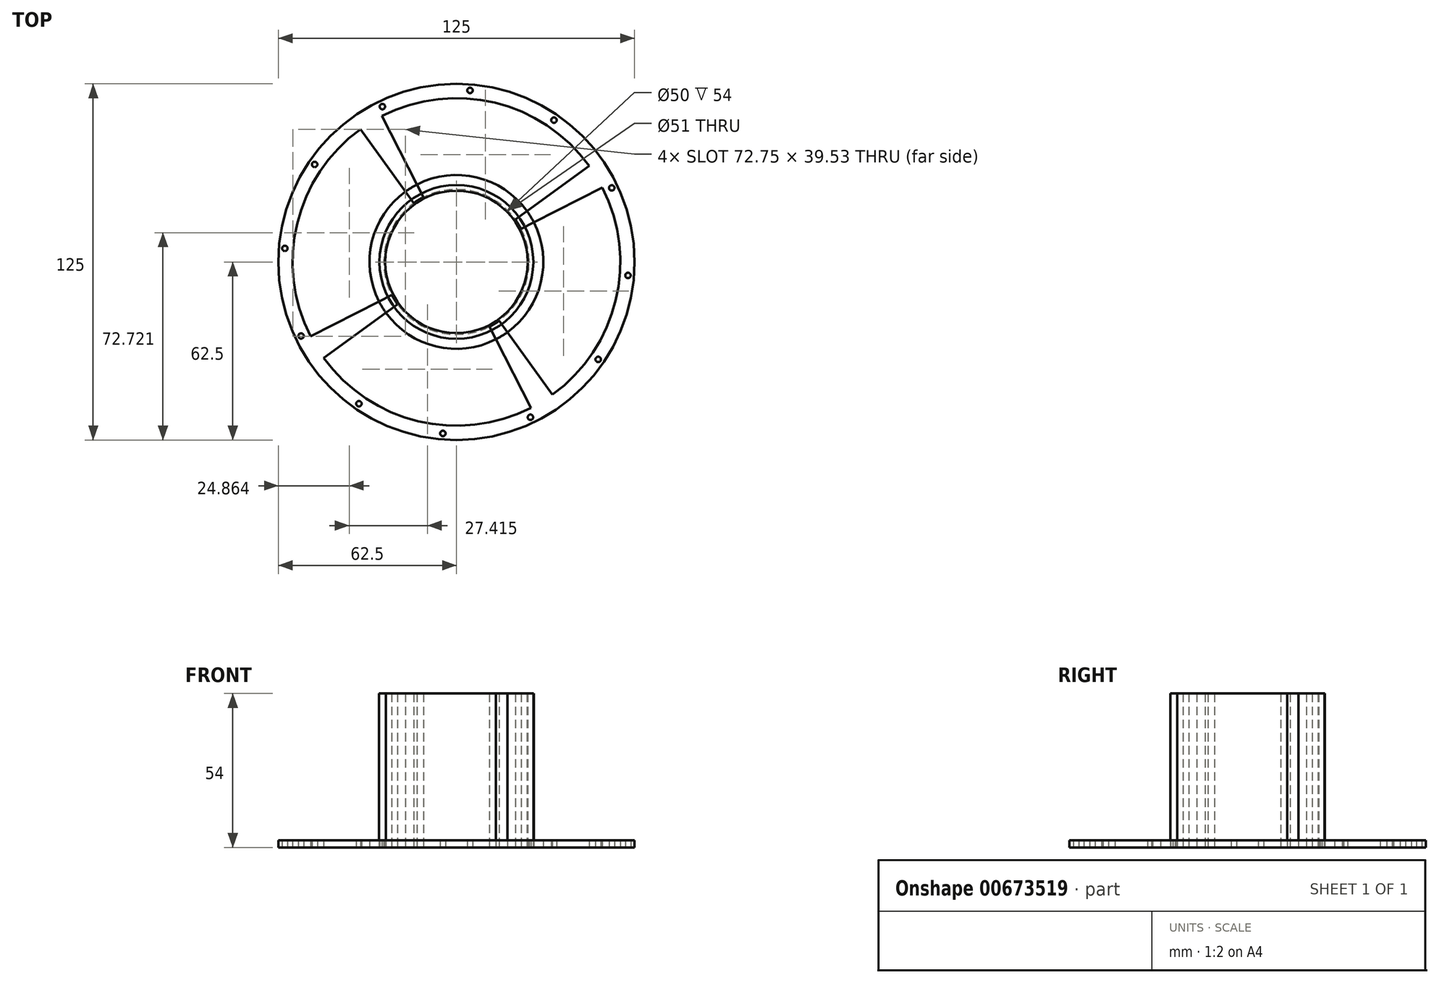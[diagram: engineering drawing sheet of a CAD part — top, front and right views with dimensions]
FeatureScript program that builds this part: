
annotation { "Feature Type Name" : "Feature", "Feature Type Description" : "" }
export const myFeature = defineFeature(function(context is Context, id is Id, definition is map)
    precondition{}
    {
        {
            var Q0;
            Q0=qCreatedBy(makeId("Top.planeOp"),FACE);
            var sketch = newSketch(context, id + "F0", { "sketchPlane" : qUnion([Q0])});
            skCircle(sketch, "E0", {"center": v(0, 0) * mm, "radius": 25.5 * mm});
            skCircle(sketch, "E1.0", {"center": v(0, 0) * mm, "radius": 30.5 * mm});
            skCircle(sketch, "E2", {"center": v(0, 0) * mm, "radius": 57.5 * mm});
            skCircle(sketch, "E3.0", {"center": v(0, 0) * mm, "radius": 62.5 * mm});
            skLineSegment(sketch, "E4", {"start": v(0, 0) * mm, "end": v(51.2, 26.15) * mm});
            skLineSegment(sketch, "E5", {"start": v(0, 0) * mm, "end": v(46.6, 33.7) * mm});
            skLineSegment(sketch, "E6.1.0", {"start": v(0, 0) * mm, "end": v(-33.7, 46.6) * mm});
            skLineSegment(sketch, "E6.1.1", {"start": v(0, 0) * mm, "end": v(-26.15, 51.2) * mm});
            skLineSegment(sketch, "E6.2.0", {"start": v(0, 0) * mm, "end": v(-46.6, -33.7) * mm});
            skLineSegment(sketch, "E6.2.1", {"start": v(0, 0) * mm, "end": v(-51.2, -26.15) * mm});
            skLineSegment(sketch, "E6.3.0", {"start": v(0, 0) * mm, "end": v(33.7, -46.6) * mm});
            skLineSegment(sketch, "E6.3.1", {"start": v(0, 0) * mm, "end": v(26.15, -51.2) * mm});
            skCircle(sketch, "E7", {"center": v(34.22, 49.76) * mm, "radius": 0.95 * mm});
            skCircle(sketch, "E8.1.0", {"center": v(4.76, 60.2) * mm, "radius": 0.95 * mm});
            skCircle(sketch, "E8.2.0", {"center": v(-25.98, 54.52) * mm, "radius": 0.95 * mm});
            skCircle(sketch, "E8.3.0", {"center": v(-49.76, 34.22) * mm, "radius": 0.95 * mm});
            skCircle(sketch, "E8.4.0", {"center": v(-60.2, 4.76) * mm, "radius": 0.95 * mm});
            skCircle(sketch, "E8.5.0", {"center": v(-54.52, -25.98) * mm, "radius": 0.95 * mm});
            skCircle(sketch, "E8.6.0", {"center": v(-34.22, -49.76) * mm, "radius": 0.95 * mm});
            skCircle(sketch, "E8.7.0", {"center": v(-4.76, -60.2) * mm, "radius": 0.95 * mm});
            skCircle(sketch, "E8.8.0", {"center": v(25.98, -54.52) * mm, "radius": 0.95 * mm});
            skCircle(sketch, "E8.9.0", {"center": v(49.76, -34.22) * mm, "radius": 0.95 * mm});
            skCircle(sketch, "E8.10.0", {"center": v(60.2, -4.76) * mm, "radius": 0.95 * mm});
            skCircle(sketch, "E8.11.0", {"center": v(54.52, 25.98) * mm, "radius": 0.95 * mm});
            skSolve(sketch);
        }
        {
            var Q0;
            Q0=makeQuery(id+"F0.imprint","IMPRINT",FACE,{"disambiguationData":[TD([[makeQuery(id+"F0.imprint","IMPRINT",EDGE,{"derivedFrom":sQuery(id+"F0.wireOp",EDGE,"E3.0")}),1.0]])]});
            var Q1;
            {var subQ0=sQuery(id+"F0.wireOp",EDGE,"E6.1.1");var subQ1=sQuery(id+"F0.wireOp",EDGE,"E1.0");var subQ2=makeQuery(id+"F0.imprint","INTERSECT",VERTEX,{"derivedFrom":[subQ1,subQ0]});Q1=makeQuery(id+"F0.imprint","IMPRINT",FACE,{"disambiguationData":[TD([[makeQuery(id+"F0.imprint","IMPRINT",EDGE,{"disambiguationData":[TD([[subQ2,-1.0]])],"derivedFrom":subQ1}),-1.0]])]});}
            var Q2;
            {var subQ0=sQuery(id+"F0.wireOp",EDGE,"E5");var subQ1=sQuery(id+"F0.wireOp",EDGE,"E1.0");var subQ2=makeQuery(id+"F0.imprint","INTERSECT",VERTEX,{"derivedFrom":[subQ1,subQ0]});Q2=makeQuery(id+"F0.imprint","IMPRINT",FACE,{"disambiguationData":[TD([[makeQuery(id+"F0.imprint","IMPRINT",EDGE,{"disambiguationData":[TD([[subQ2,1.0]])],"derivedFrom":subQ1}),-1.0]])]});}
            var Q3;
            {var subQ0=sQuery(id+"F0.wireOp",EDGE,"E6.2.1");var subQ1=sQuery(id+"F0.wireOp",EDGE,"E1.0");var subQ2=makeQuery(id+"F0.imprint","INTERSECT",VERTEX,{"derivedFrom":[subQ1,subQ0]});Q3=makeQuery(id+"F0.imprint","IMPRINT",FACE,{"disambiguationData":[TD([[makeQuery(id+"F0.imprint","IMPRINT",EDGE,{"disambiguationData":[TD([[subQ2,-1.0]])],"derivedFrom":subQ1}),-1.0]])]});}
            var Q4;
            {var subQ0=sQuery(id+"F0.wireOp",EDGE,"E6.3.1");var subQ1=sQuery(id+"F0.wireOp",EDGE,"E1.0");var subQ2=makeQuery(id+"F0.imprint","INTERSECT",VERTEX,{"derivedFrom":[subQ1,subQ0]});Q4=makeQuery(id+"F0.imprint","IMPRINT",FACE,{"disambiguationData":[TD([[makeQuery(id+"F0.imprint","IMPRINT",EDGE,{"disambiguationData":[TD([[subQ2,-1.0]])],"derivedFrom":subQ1}),-1.0]])]});}
            var Q5;
            {var subQ0=sQuery(id+"F0.wireOp",EDGE,"E6.2.1");var subQ1=sQuery(id+"F0.wireOp",EDGE,"E0");var subQ2=makeQuery(id+"F0.imprint","INTERSECT",VERTEX,{"derivedFrom":[subQ1,subQ0]});Q5=makeQuery(id+"F0.imprint","IMPRINT",FACE,{"disambiguationData":[TD([[makeQuery(id+"F0.imprint","IMPRINT",EDGE,{"disambiguationData":[TD([[subQ2,-1.0]])],"derivedFrom":subQ1}),-1.0]])]});}
            var Q6;
            {var subQ0=sQuery(id+"F0.wireOp",EDGE,"E6.1.0");var subQ1=sQuery(id+"F0.wireOp",EDGE,"E0");var subQ2=makeQuery(id+"F0.imprint","INTERSECT",VERTEX,{"derivedFrom":[subQ1,subQ0]});Q6=makeQuery(id+"F0.imprint","IMPRINT",FACE,{"disambiguationData":[TD([[makeQuery(id+"F0.imprint","IMPRINT",EDGE,{"disambiguationData":[TD([[subQ2,-1.0]])],"derivedFrom":subQ1}),-1.0]])]});}
            var Q7;
            {var subQ0=sQuery(id+"F0.wireOp",EDGE,"E4");var subQ1=sQuery(id+"F0.wireOp",EDGE,"E0");var subQ2=makeQuery(id+"F0.imprint","INTERSECT",VERTEX,{"derivedFrom":[subQ1,subQ0]});Q7=makeQuery(id+"F0.imprint","IMPRINT",FACE,{"disambiguationData":[TD([[makeQuery(id+"F0.imprint","IMPRINT",EDGE,{"disambiguationData":[TD([[subQ2,1.0]])],"derivedFrom":subQ1}),-1.0]])]});}
            var Q8;
            {var subQ0=sQuery(id+"F0.wireOp",EDGE,"E6.3.1");var subQ1=sQuery(id+"F0.wireOp",EDGE,"E0");var subQ2=makeQuery(id+"F0.imprint","INTERSECT",VERTEX,{"derivedFrom":[subQ1,subQ0]});Q8=makeQuery(id+"F0.imprint","IMPRINT",FACE,{"disambiguationData":[TD([[makeQuery(id+"F0.imprint","IMPRINT",EDGE,{"disambiguationData":[TD([[subQ2,-1.0]])],"derivedFrom":subQ1}),-1.0]])]});}
            var Q9;
            {var subQ0=sQuery(id+"F0.wireOp",EDGE,"E5");var subQ1=sQuery(id+"F0.wireOp",EDGE,"E0");var subQ2=makeQuery(id+"F0.imprint","INTERSECT",VERTEX,{"derivedFrom":[subQ1,subQ0]});Q9=makeQuery(id+"F0.imprint","IMPRINT",FACE,{"disambiguationData":[TD([[makeQuery(id+"F0.imprint","IMPRINT",EDGE,{"disambiguationData":[TD([[subQ2,1.0]])],"derivedFrom":subQ1}),-1.0]])]});}
            var Q10;
            {var subQ0=sQuery(id+"F0.wireOp",EDGE,"E5");var subQ1=sQuery(id+"F0.wireOp",EDGE,"E0");var subQ2=makeQuery(id+"F0.imprint","INTERSECT",VERTEX,{"derivedFrom":[subQ1,subQ0]});Q10=makeQuery(id+"F0.imprint","IMPRINT",FACE,{"disambiguationData":[TD([[makeQuery(id+"F0.imprint","IMPRINT",EDGE,{"disambiguationData":[TD([[subQ2,-1.0]])],"derivedFrom":subQ1}),-1.0]])]});}
            var Q11;
            {var subQ0=sQuery(id+"F0.wireOp",EDGE,"E6.1.1");var subQ1=sQuery(id+"F0.wireOp",EDGE,"E0");var subQ2=makeQuery(id+"F0.imprint","INTERSECT",VERTEX,{"derivedFrom":[subQ1,subQ0]});Q11=makeQuery(id+"F0.imprint","IMPRINT",FACE,{"disambiguationData":[TD([[makeQuery(id+"F0.imprint","IMPRINT",EDGE,{"disambiguationData":[TD([[subQ2,-1.0]])],"derivedFrom":subQ1}),-1.0]])]});}
            var Q12;
            {var subQ0=sQuery(id+"F0.wireOp",EDGE,"E6.2.0");var subQ1=sQuery(id+"F0.wireOp",EDGE,"E0");var subQ2=makeQuery(id+"F0.imprint","INTERSECT",VERTEX,{"derivedFrom":[subQ1,subQ0]});Q12=makeQuery(id+"F0.imprint","IMPRINT",FACE,{"disambiguationData":[TD([[makeQuery(id+"F0.imprint","IMPRINT",EDGE,{"disambiguationData":[TD([[subQ2,-1.0]])],"derivedFrom":subQ1}),-1.0]])]});}
            extrude(context, id + "F1", {"entities" : qUnion([Q0, Q1, Q2, Q3, Q4, Q5, Q6, Q7, Q8, Q9, Q10, Q11, Q12]), "depth" : 2.5 * mm, "offsetDistance" : 25 * mm});
        }
        {
            var Q0;
            {var subQ0=sQuery(id+"F0.wireOp",EDGE,"E6.1.1");var subQ1=sQuery(id+"F0.wireOp",EDGE,"E0");var subQ2=makeQuery(id+"F0.imprint","INTERSECT",VERTEX,{"derivedFrom":[subQ1,subQ0]});Q0=makeQuery(id+"F0.imprint","IMPRINT",FACE,{"disambiguationData":[TD([[makeQuery(id+"F0.imprint","IMPRINT",EDGE,{"disambiguationData":[TD([[subQ2,-1.0]])],"derivedFrom":subQ1}),-1.0]])]});}
            var Q1;
            {var subQ0=sQuery(id+"F0.wireOp",EDGE,"E5");var subQ1=sQuery(id+"F0.wireOp",EDGE,"E0");var subQ2=makeQuery(id+"F0.imprint","INTERSECT",VERTEX,{"derivedFrom":[subQ1,subQ0]});Q1=makeQuery(id+"F0.imprint","IMPRINT",FACE,{"disambiguationData":[TD([[makeQuery(id+"F0.imprint","IMPRINT",EDGE,{"disambiguationData":[TD([[subQ2,1.0]])],"derivedFrom":subQ1}),-1.0]])]});}
            var Q2;
            {var subQ0=sQuery(id+"F0.wireOp",EDGE,"E6.2.1");var subQ1=sQuery(id+"F0.wireOp",EDGE,"E0");var subQ2=makeQuery(id+"F0.imprint","INTERSECT",VERTEX,{"derivedFrom":[subQ1,subQ0]});Q2=makeQuery(id+"F0.imprint","IMPRINT",FACE,{"disambiguationData":[TD([[makeQuery(id+"F0.imprint","IMPRINT",EDGE,{"disambiguationData":[TD([[subQ2,-1.0]])],"derivedFrom":subQ1}),-1.0]])]});}
            var Q3;
            {var subQ0=sQuery(id+"F0.wireOp",EDGE,"E6.3.1");var subQ1=sQuery(id+"F0.wireOp",EDGE,"E0");var subQ2=makeQuery(id+"F0.imprint","INTERSECT",VERTEX,{"derivedFrom":[subQ1,subQ0]});Q3=makeQuery(id+"F0.imprint","IMPRINT",FACE,{"disambiguationData":[TD([[makeQuery(id+"F0.imprint","IMPRINT",EDGE,{"disambiguationData":[TD([[subQ2,-1.0]])],"derivedFrom":subQ1}),-1.0]])]});}
            extrude(context, id + "F2", {"entities" : qUnion([Q0, Q1, Q2, Q3]), "depth" : 54 * mm, "offsetDistance" : 25 * mm});
        }
        {
            var Q0;
            {var subQ0=sQuery(id+"F0.wireOp",EDGE,"E5");var subQ1=sQuery(id+"F0.wireOp",EDGE,"E0");var subQ2=makeQuery(id+"F0.imprint","INTERSECT",VERTEX,{"derivedFrom":[subQ1,subQ0]});Q0=makeQuery(id+"F0.imprint","IMPRINT",FACE,{"disambiguationData":[TD([[makeQuery(id+"F0.imprint","IMPRINT",EDGE,{"disambiguationData":[TD([[subQ2,-1.0]])],"derivedFrom":subQ1}),1.0]])]});}
            var sketch = newSketch(context, id + "F3", { "sketchPlane" : qUnion([Q0])});
            skCircle(sketch, "E9", {"center": v(0, 0) * mm, "radius": 25 * mm});
            skCircle(sketch, "E10.0", {"center": v(0, 0) * mm, "radius": 27 * mm});
            skSolve(sketch);
        }
        {
            var Q0;
            Q0 = qSketchRegion(id + "F3", true);
            extrude(context, id + "F4", {"entities" : qUnion([Q0]), "depth" : 54 * mm, "offsetDistance" : 25 * mm});
        }
    });
